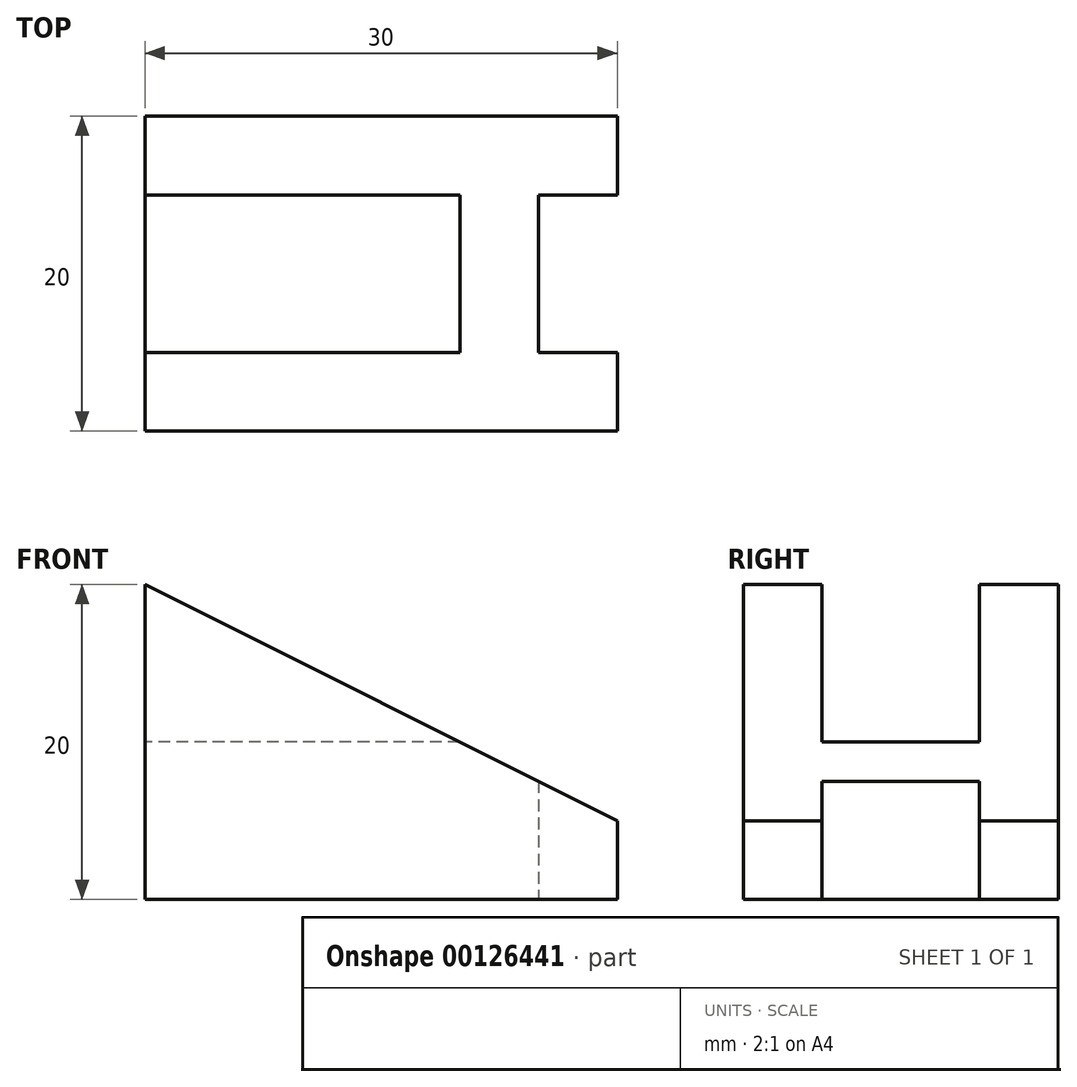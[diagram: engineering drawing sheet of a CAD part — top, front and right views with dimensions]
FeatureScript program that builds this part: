
annotation { "Feature Type Name" : "Feature", "Feature Type Description" : "" }
export const myFeature = defineFeature(function(context is Context, id is Id, definition is map)
    precondition{}
    {
        {
            var Q0;
            Q0=qCreatedBy(makeId("Front.planeOp"),FACE);
            var sketch = newSketch(context, id + "F0", { "sketchPlane" : qUnion([Q0])});
            skLineSegment(sketch, "E0", {"start": v(0, 0) * mm, "end": v(30, 0) * mm});
            skLineSegment(sketch, "E1", {"start": v(30, 0) * mm, "end": v(30, 5) * mm});
            skLineSegment(sketch, "E2", {"start": v(30, 5) * mm, "end": v(0, 20) * mm});
            skLineSegment(sketch, "E3", {"start": v(0, 20) * mm, "end": v(0, 0) * mm});
            skSolve(sketch);
        }
        {
            var Q0;
            Q0=qSketchRegion(id+"F0",true);
            extrude(context, id + "F1", {"entities" : qUnion([Q0]), "endBound" : BoundingType.SYMMETRIC, "depth" : 20 * mm});
        }
        {
            var Q0;
            Q0=makeQuery(id+"F1.opExtrude","SWEPT_FACE",FACE,{"disambiguationData":[OSD([sQuery(id+"F0.wireOp",EDGE,"E3")])]});
            var sketch = newSketch(context, id + "F2", { "sketchPlane" : qUnion([Q0])});
            skLineSegment(sketch, "E4.bottom", {"start": v(5, 10) * mm, "end": v(-5, 10) * mm});
            skLineSegment(sketch, "E4.top", {"start": v(5, 30) * mm, "end": v(-5, 30) * mm});
            skLineSegment(sketch, "E4.left", {"start": v(5, 10) * mm, "end": v(5, 30) * mm});
            skLineSegment(sketch, "E4.right", {"start": v(-5, 10) * mm, "end": v(-5, 30) * mm});
            skPoint(sketch, "E4.middle", {"position": v(0, 20) * mm});
            skSolve(sketch);
        }
        {
            var Q0;
            Q0=qSketchRegion(id+"F2",true);
            var Q1;
            Q1=makeQuery(id+"F1.opExtrude","SWEPT_FACE",FACE,{"disambiguationData":[OSD([sQuery(id+"F0.wireOp",EDGE,"E2")])]});
            extrude(context, id + "F3", {"entities" : qUnion([Q0]), "operationType" : NewBodyOperationType.REMOVE, "endBound" : BoundingType.UP_TO_SURFACE, "oppositeDirection" : true, "endBoundEntityFace" : qUnion([Q1]), "depth" : 25 * mm});
        }
        {
            var Q0;
            Q0=makeQuery(id+"F1.opExtrude","SWEPT_FACE",FACE,{"disambiguationData":[OSD([sQuery(id+"F0.wireOp",EDGE,"E0")])]});
            var sketch = newSketch(context, id + "F4", { "sketchPlane" : qUnion([Q0])});
            skLineSegment(sketch, "E5.bottom", {"start": v(35, -5) * mm, "end": v(25, -5) * mm});
            skLineSegment(sketch, "E5.top", {"start": v(35, 5) * mm, "end": v(25, 5) * mm});
            skLineSegment(sketch, "E5.left", {"start": v(35, -5) * mm, "end": v(35, 5) * mm});
            skLineSegment(sketch, "E5.right", {"start": v(25, -5) * mm, "end": v(25, 5) * mm});
            skPoint(sketch, "E5.middle", {"position": v(30, 0) * mm});
            skSolve(sketch);
        }
        {
            var Q0;
            Q0=qSketchRegion(id+"F4",true);
            var Q1;
            Q1=makeQuery(id+"F1.opExtrude","SWEPT_FACE",FACE,{"disambiguationData":[OSD([sQuery(id+"F0.wireOp",EDGE,"E2")])]});
            extrude(context, id + "F5", {"entities" : qUnion([Q0]), "operationType" : NewBodyOperationType.REMOVE, "endBound" : BoundingType.UP_TO_SURFACE, "oppositeDirection" : true, "endBoundEntityFace" : qUnion([Q1]), "depth" : 25 * mm});
        }
    });
